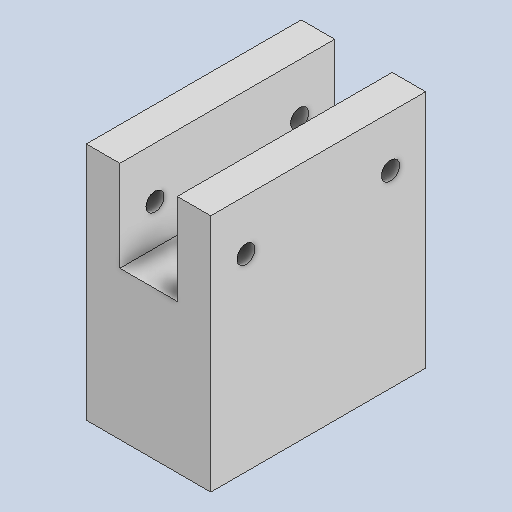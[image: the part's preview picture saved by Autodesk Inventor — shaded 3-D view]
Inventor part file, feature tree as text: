
AUTODESK INVENTOR PART (.ipt)
format: ipt  version: 2024.3 (Build 283343000, 343)  size: 228,864 bytes
history: native  units: mm
features: extrude x4, sketch x4, reference x4, other x3, projected_geometry x1
ambient origin geometry x8: Origin, YZ Plane, XZ Plane, XY Plane, X Axis, Y Axis, Z Axis, Center Point
bodies: Solid1 (feature_tree)
feature tree (16):
  extrude  "Extrusion1"  Depth=44.9mm
  extrude  "Extrusion2"  Depth=50.0mm
  extrude  "Extrusion3"  Depth=12.0mm
  extrude  "Extrusion4"  Depth=12.0mm
  sketch  "Sketch1"  dims[d0=26.0mm d1=44.9mm]
  sketch  "Sketch2"  dims[d2=50.0mm d3=0.0mm d4=6.0mm]
  projected_geometry  "Projected Loop1"
  sketch  "Sketch3"  dims[d5=19.0mm d6=12.0mm]
  sketch  "Sketch4"  dims[d7=50.0mm d8=0.0mm d9=3.8mm d13=50.0mm d14=0.0mm d15=12.0mm d16=0.0mm]
  reference  "Reference1"
  reference  "Reference2"
  reference  "Reference3"
  reference  "Reference4"
  other  "<userpath>\Desktop\Unal\Robotica\proyecto\garra neumatica\Assembly1.iam"
  other  "Assembly1.iam"
  other  "conexión:1"
